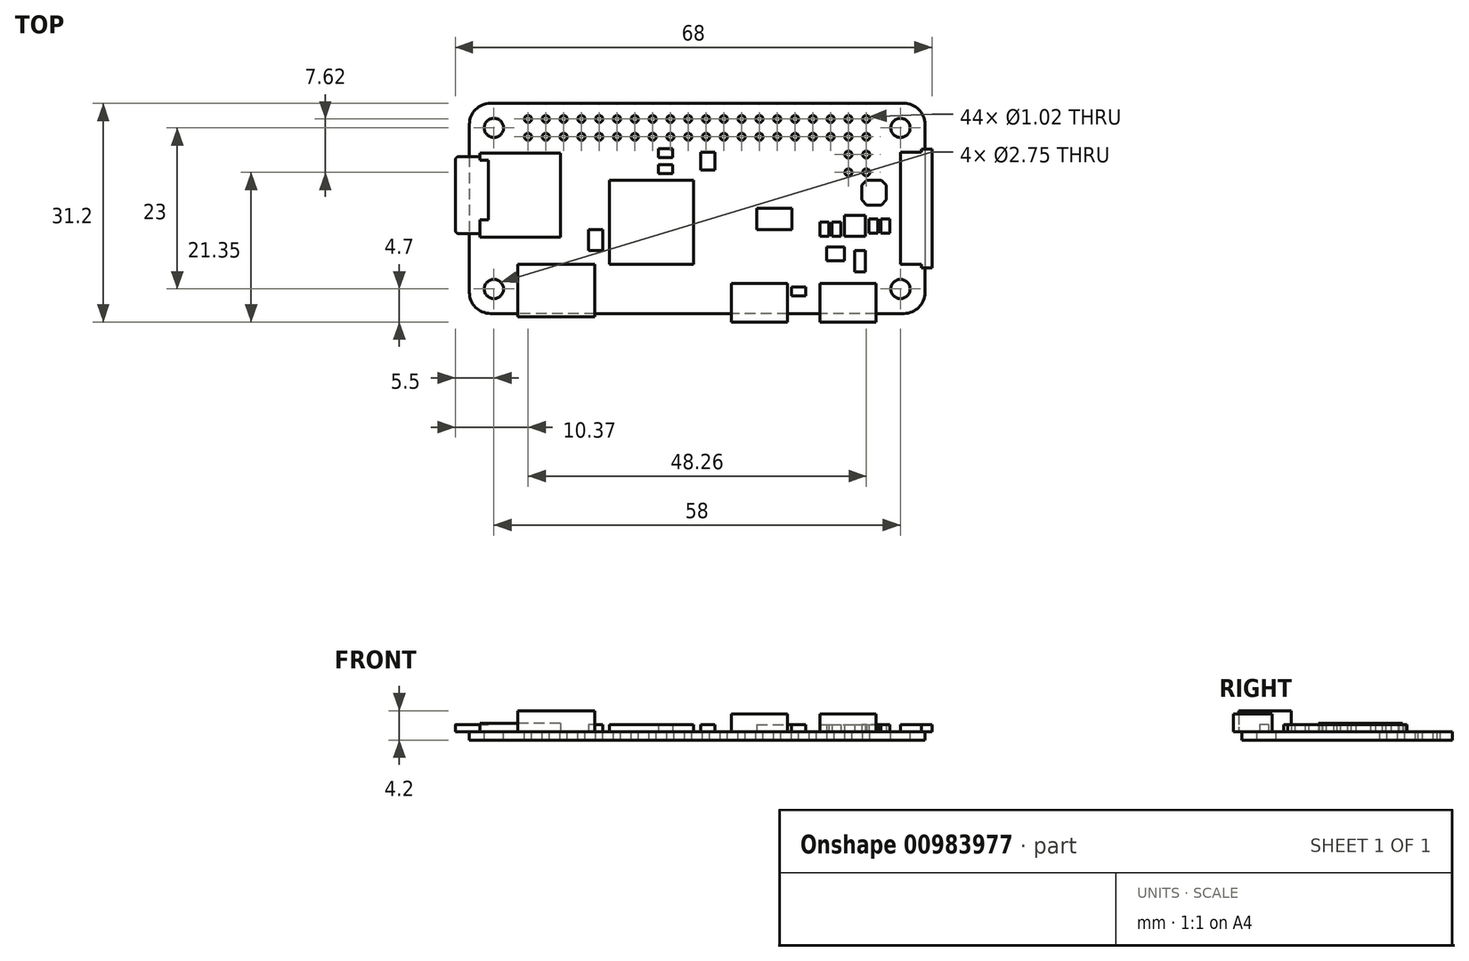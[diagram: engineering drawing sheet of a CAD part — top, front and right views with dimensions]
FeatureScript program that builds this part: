
annotation { "Feature Type Name" : "Feature", "Feature Type Description" : "" }
export const myFeature = defineFeature(function(context is Context, id is Id, definition is map)
    precondition{}
    {
        {
            var Q0;
            Q0=qCreatedBy(makeId("Top.planeOp"),FACE);
            var sketch = newSketch(context, id + "F0", { "sketchPlane" : qUnion([Q0])});
            skLineSegment(sketch, "E0.bottom", {"start": v(29.5, 15) * mm, "end": v(-29.5, 15) * mm});
            skLineSegment(sketch, "E0.top", {"start": v(29.5, -15) * mm, "end": v(-29.5, -15) * mm});
            skLineSegment(sketch, "E0.left", {"start": v(32.5, 12) * mm, "end": v(32.5, -12) * mm});
            skLineSegment(sketch, "E0.right", {"start": v(-32.5, 12) * mm, "end": v(-32.5, -12) * mm});
            skPoint(sketch, "E0.middle", {"position": v(0, 0) * mm});
            skPoint(sketch, "E1.visualSharp", {"position": v(-32.5, 15) * mm});
            skArc(sketch, "E1.filletArc", {"start": v(-29.5, 15) * mm, "mid": v(-31.62, 14.12) * mm, "end": v(-32.5, 12) * mm});
            skPoint(sketch, "E2.visualSharp", {"position": v(32.5, 15) * mm});
            skArc(sketch, "E2.filletArc", {"start": v(32.5, 12) * mm, "mid": v(31.62, 14.12) * mm, "end": v(29.5, 15) * mm});
            skPoint(sketch, "E3.visualSharp", {"position": v(32.5, -15) * mm});
            skArc(sketch, "E3.filletArc", {"start": v(29.5, -15) * mm, "mid": v(31.62, -14.12) * mm, "end": v(32.5, -12) * mm});
            skPoint(sketch, "E4.visualSharp", {"position": v(-32.5, -15) * mm});
            skArc(sketch, "E4.filletArc", {"start": v(-32.5, -12) * mm, "mid": v(-31.62, -14.12) * mm, "end": v(-29.5, -15) * mm});
            skLineSegment(sketch, "E5.bottom", {"start": v(29, 11.5) * mm, "end": v(-29, 11.5) * mm, "construction": true});
            skLineSegment(sketch, "E5.top", {"start": v(29, -11.5) * mm, "end": v(-29, -11.5) * mm, "construction": true});
            skLineSegment(sketch, "E5.left", {"start": v(29, 11.5) * mm, "end": v(29, -11.5) * mm, "construction": true});
            skLineSegment(sketch, "E5.right", {"start": v(-29, 11.5) * mm, "end": v(-29, -11.5) * mm, "construction": true});
            skCircle(sketch, "E6", {"center": v(29, 11.5) * mm, "radius": 3 * mm});
            skCircle(sketch, "E7", {"center": v(29, 11.5) * mm, "radius": 1.38 * mm});
            skCircle(sketch, "E8", {"center": v(-29, 11.5) * mm, "radius": 1.38 * mm});
            skCircle(sketch, "E9", {"center": v(-29, 11.5) * mm, "radius": 3 * mm});
            skCircle(sketch, "E10", {"center": v(-29, -11.5) * mm, "radius": 3 * mm});
            skCircle(sketch, "E11", {"center": v(-29, -11.5) * mm, "radius": 1.38 * mm});
            skCircle(sketch, "E12", {"center": v(29, -11.5) * mm, "radius": 1.38 * mm});
            skCircle(sketch, "E13", {"center": v(29, -11.5) * mm, "radius": 3 * mm});
            skCircle(sketch, "E14", {"center": v(24.13, 12.77) * mm, "radius": 0.5 * mm});
            skCircle(sketch, "E15", {"center": v(24.13, 10.23) * mm, "radius": 0.5 * mm});
            skLineSegment(sketch, "E16", {"start": v(24.13, 12.77) * mm, "end": v(24.13, 10.23) * mm, "construction": true});
            skPoint(sketch, "E17", {"position": v(24.13, 11.5) * mm});
            skCircle(sketch, "E18.1.0.0", {"center": v(21.59, 12.77) * mm, "radius": 0.5 * mm});
            skCircle(sketch, "E18.1.0.1", {"center": v(21.59, 10.23) * mm, "radius": 0.5 * mm});
            skCircle(sketch, "E18.2.0.0", {"center": v(19.05, 12.77) * mm, "radius": 0.5 * mm});
            skCircle(sketch, "E18.2.0.1", {"center": v(19.05, 10.23) * mm, "radius": 0.5 * mm});
            skCircle(sketch, "E18.3.0.0", {"center": v(16.5, 12.77) * mm, "radius": 0.5 * mm});
            skCircle(sketch, "E18.3.0.1", {"center": v(16.5, 10.23) * mm, "radius": 0.5 * mm});
            skCircle(sketch, "E18.4.0.0", {"center": v(13.97, 12.77) * mm, "radius": 0.5 * mm});
            skCircle(sketch, "E18.4.0.1", {"center": v(13.97, 10.23) * mm, "radius": 0.5 * mm});
            skCircle(sketch, "E18.5.0.0", {"center": v(11.43, 12.77) * mm, "radius": 0.5 * mm});
            skCircle(sketch, "E18.5.0.1", {"center": v(11.43, 10.23) * mm, "radius": 0.5 * mm});
            skCircle(sketch, "E18.6.0.0", {"center": v(8.89, 12.77) * mm, "radius": 0.5 * mm});
            skCircle(sketch, "E18.6.0.1", {"center": v(8.89, 10.23) * mm, "radius": 0.5 * mm});
            skCircle(sketch, "E18.7.0.0", {"center": v(6.35, 12.77) * mm, "radius": 0.5 * mm});
            skCircle(sketch, "E18.7.0.1", {"center": v(6.35, 10.23) * mm, "radius": 0.5 * mm});
            skCircle(sketch, "E18.8.0.0", {"center": v(3.8, 12.77) * mm, "radius": 0.5 * mm});
            skCircle(sketch, "E18.8.0.1", {"center": v(3.8, 10.23) * mm, "radius": 0.5 * mm});
            skCircle(sketch, "E18.9.0.0", {"center": v(1.27, 12.77) * mm, "radius": 0.5 * mm});
            skCircle(sketch, "E18.9.0.1", {"center": v(1.27, 10.23) * mm, "radius": 0.5 * mm});
            skCircle(sketch, "E18.10.0.0", {"center": v(-1.27, 12.77) * mm, "radius": 0.5 * mm});
            skCircle(sketch, "E18.10.0.1", {"center": v(-1.27, 10.23) * mm, "radius": 0.5 * mm});
            skCircle(sketch, "E18.11.0.0", {"center": v(-3.81, 12.77) * mm, "radius": 0.5 * mm});
            skCircle(sketch, "E18.11.0.1", {"center": v(-3.81, 10.23) * mm, "radius": 0.5 * mm});
            skCircle(sketch, "E18.12.0.0", {"center": v(-6.35, 12.77) * mm, "radius": 0.5 * mm});
            skCircle(sketch, "E18.12.0.1", {"center": v(-6.35, 10.23) * mm, "radius": 0.5 * mm});
            skCircle(sketch, "E18.13.0.0", {"center": v(-8.9, 12.77) * mm, "radius": 0.5 * mm});
            skCircle(sketch, "E18.13.0.1", {"center": v(-8.9, 10.23) * mm, "radius": 0.5 * mm});
            skCircle(sketch, "E18.14.0.0", {"center": v(-11.43, 12.77) * mm, "radius": 0.5 * mm});
            skCircle(sketch, "E18.14.0.1", {"center": v(-11.43, 10.23) * mm, "radius": 0.5 * mm});
            skCircle(sketch, "E18.15.0.0", {"center": v(-13.97, 12.77) * mm, "radius": 0.5 * mm});
            skCircle(sketch, "E18.15.0.1", {"center": v(-13.97, 10.23) * mm, "radius": 0.5 * mm});
            skCircle(sketch, "E18.16.0.0", {"center": v(-16.51, 12.77) * mm, "radius": 0.5 * mm});
            skCircle(sketch, "E18.16.0.1", {"center": v(-16.51, 10.23) * mm, "radius": 0.5 * mm});
            skCircle(sketch, "E18.17.0.0", {"center": v(-19.05, 12.77) * mm, "radius": 0.5 * mm});
            skCircle(sketch, "E18.17.0.1", {"center": v(-19.05, 10.23) * mm, "radius": 0.5 * mm});
            skCircle(sketch, "E18.18.0.0", {"center": v(-21.6, 12.77) * mm, "radius": 0.5 * mm});
            skCircle(sketch, "E18.18.0.1", {"center": v(-21.6, 10.23) * mm, "radius": 0.5 * mm});
            skCircle(sketch, "E18.19.0.0", {"center": v(-24.13, 12.77) * mm, "radius": 0.5 * mm});
            skCircle(sketch, "E18.19.0.1", {"center": v(-24.13, 10.23) * mm, "radius": 0.5 * mm});
            skLineSegment(sketch, "E18.direction1", {"start": v(24.13, 12.77) * mm, "end": v(21.59, 12.77) * mm, "construction": true});
            skCircle(sketch, "E19.1.0.0", {"center": v(21.59, 7.69) * mm, "radius": 0.5 * mm});
            skCircle(sketch, "E19.1.0.1", {"center": v(24.13, 7.69) * mm, "radius": 0.5 * mm});
            skCircle(sketch, "E19.1.0.2", {"center": v(24.13, 5.15) * mm, "radius": 0.5 * mm});
            skCircle(sketch, "E19.1.0.3", {"center": v(21.59, 5.15) * mm, "radius": 0.5 * mm});
            skLineSegment(sketch, "E19.direction1", {"start": v(21.59, 12.77) * mm, "end": v(21.59, 7.69) * mm, "construction": true});
            skSolve(sketch);
        }
        {
            var Q0;
            Q0=qCreatedBy(makeId("Top.planeOp"),FACE);
            var sketch = newSketch(context, id + "F1", { "sketchPlane" : qUnion([Q0])});
            skLineSegment(sketch, "E20.bottom", {"start": v(33.5, -8.5) * mm, "end": v(32, -8.5) * mm});
            skLineSegment(sketch, "E20.top", {"start": v(33.5, 8.5) * mm, "end": v(32, 8.5) * mm});
            skLineSegment(sketch, "E20.left", {"start": v(33.5, -8.5) * mm, "end": v(33.5, 8.5) * mm});
            skLineSegment(sketch, "E20.right", {"start": v(32, -8.5) * mm, "end": v(32, 8.5) * mm});
            skPoint(sketch, "E20.middle", {"position": v(32.75, 0) * mm});
            skLineSegment(sketch, "E21.bottom", {"start": v(-14.6, -15.5) * mm, "end": v(-25.6, -15.5) * mm});
            skLineSegment(sketch, "E21.top", {"start": v(-14.6, -8) * mm, "end": v(-25.6, -8) * mm});
            skLineSegment(sketch, "E21.left", {"start": v(-14.6, -15.5) * mm, "end": v(-14.6, -8) * mm});
            skLineSegment(sketch, "E21.right", {"start": v(-25.6, -15.5) * mm, "end": v(-25.6, -8) * mm});
            skPoint(sketch, "E21.middle", {"position": v(-20.1, -11.75) * mm});
            skLineSegment(sketch, "E22.bottom", {"start": v(12.9, -16.2) * mm, "end": v(4.9, -16.2) * mm});
            skLineSegment(sketch, "E22.top", {"start": v(12.9, -10.7) * mm, "end": v(4.9, -10.7) * mm});
            skLineSegment(sketch, "E22.left", {"start": v(12.9, -16.2) * mm, "end": v(12.9, -10.7) * mm});
            skLineSegment(sketch, "E22.right", {"start": v(4.9, -16.2) * mm, "end": v(4.9, -10.7) * mm});
            skPoint(sketch, "E22.middle", {"position": v(8.9, -13.45) * mm});
            skLineSegment(sketch, "E23.bottom", {"start": v(25.5, -16.2) * mm, "end": v(17.5, -16.2) * mm});
            skLineSegment(sketch, "E23.top", {"start": v(25.5, -10.7) * mm, "end": v(17.5, -10.7) * mm});
            skLineSegment(sketch, "E23.left", {"start": v(25.5, -16.2) * mm, "end": v(25.5, -10.7) * mm});
            skLineSegment(sketch, "E23.right", {"start": v(17.5, -16.2) * mm, "end": v(17.5, -10.7) * mm});
            skPoint(sketch, "E23.middle", {"position": v(21.5, -13.45) * mm});
            skLineSegment(sketch, "E24.bottom", {"start": v(-19.5, 7.9) * mm, "end": v(-31, 7.9) * mm});
            skLineSegment(sketch, "E24.top", {"start": v(-19.5, -4.1) * mm, "end": v(-31, -4.1) * mm});
            skLineSegment(sketch, "E24.left", {"start": v(-19.5, 7.9) * mm, "end": v(-19.5, -4.1) * mm});
            skLineSegment(sketch, "E24.right", {"start": v(-31, 7.9) * mm, "end": v(-31, -4.1) * mm});
            skPoint(sketch, "E24.middle", {"position": v(-25.25, 1.9) * mm});
            skLineSegment(sketch, "E25", {"start": v(-31, 7.4) * mm, "end": v(-34, 7.4) * mm});
            skLineSegment(sketch, "E26", {"start": v(-34.5, 6.9) * mm, "end": v(-34.5, -3.1) * mm});
            skLineSegment(sketch, "E27", {"start": v(-34, -3.6) * mm, "end": v(-31, -3.6) * mm});
            skPoint(sketch, "E28.visualSharp", {"position": v(-34.5, 7.4) * mm});
            skArc(sketch, "E28.filletArc", {"start": v(-34, 7.4) * mm, "mid": v(-34.35, 7.25) * mm, "end": v(-34.5, 6.9) * mm});
            skPoint(sketch, "E29.visualSharp", {"position": v(-34.5, -3.6) * mm});
            skArc(sketch, "E29.filletArc", {"start": v(-34.5, -3.1) * mm, "mid": v(-34.35, -3.45) * mm, "end": v(-34, -3.6) * mm});
            skPoint(sketch, "E30", {"position": v(-34.5, 1.9) * mm});
            skLineSegment(sketch, "E31", {"start": v(-31, 6.9) * mm, "end": v(-29.8, 6.9) * mm});
            skLineSegment(sketch, "E32", {"start": v(-29.8, 6.9) * mm, "end": v(-29.8, -1.6) * mm});
            skLineSegment(sketch, "E33", {"start": v(-29.8, -1.6) * mm, "end": v(-31, -1.6) * mm});
            skLineSegment(sketch, "E34", {"start": v(32, 8) * mm, "end": v(29, 8) * mm});
            skLineSegment(sketch, "E35", {"start": v(29, 8) * mm, "end": v(29, -8) * mm});
            skLineSegment(sketch, "E36", {"start": v(29, -8) * mm, "end": v(32, -8) * mm});
            skLineSegment(sketch, "E37", {"start": v(32.75, 0) * mm, "end": v(29, 0) * mm, "construction": true});
            skSolve(sketch);
        }
        {
            var Q0;
            Q0=qCreatedBy(makeId("Top.planeOp"),FACE);
            var sketch = newSketch(context, id + "F2", { "sketchPlane" : qUnion([Q0])});
            skLineSegment(sketch, "E38.bottom", {"start": v(-12.5, -8) * mm, "end": v(-0.5, -8) * mm});
            skLineSegment(sketch, "E38.top", {"start": v(-12.5, 4) * mm, "end": v(-0.5, 4) * mm});
            skLineSegment(sketch, "E38.left", {"start": v(-12.5, -8) * mm, "end": v(-12.5, 4) * mm});
            skLineSegment(sketch, "E38.right", {"start": v(-0.5, -8) * mm, "end": v(-0.5, 4) * mm});
            skLineSegment(sketch, "E39.bottom", {"start": v(-5.53, 8.54) * mm, "end": v(-3.5, 8.54) * mm});
            skLineSegment(sketch, "E39.top", {"start": v(-5.53, 7.27) * mm, "end": v(-3.5, 7.27) * mm});
            skLineSegment(sketch, "E39.left", {"start": v(-5.53, 8.54) * mm, "end": v(-5.53, 7.27) * mm});
            skLineSegment(sketch, "E39.right", {"start": v(-3.5, 8.54) * mm, "end": v(-3.5, 7.27) * mm});
            skLineSegment(sketch, "E40.bottom", {"start": v(-5.53, 6.27) * mm, "end": v(-3.5, 6.27) * mm});
            skLineSegment(sketch, "E40.top", {"start": v(-5.53, 5) * mm, "end": v(-3.5, 5) * mm});
            skLineSegment(sketch, "E40.left", {"start": v(-5.53, 6.27) * mm, "end": v(-5.53, 5) * mm});
            skLineSegment(sketch, "E40.right", {"start": v(-3.5, 6.27) * mm, "end": v(-3.5, 5) * mm});
            skLineSegment(sketch, "E41.bottom", {"start": v(13.47, -11.23) * mm, "end": v(15.5, -11.23) * mm});
            skLineSegment(sketch, "E41.top", {"start": v(13.47, -12.5) * mm, "end": v(15.5, -12.5) * mm});
            skLineSegment(sketch, "E41.left", {"start": v(13.47, -11.23) * mm, "end": v(13.47, -12.5) * mm});
            skLineSegment(sketch, "E41.right", {"start": v(15.5, -11.23) * mm, "end": v(15.5, -12.5) * mm});
            skLineSegment(sketch, "E42.bottom", {"start": v(17.5, -1.97) * mm, "end": v(18.77, -1.97) * mm});
            skLineSegment(sketch, "E42.top", {"start": v(17.5, -4) * mm, "end": v(18.77, -4) * mm});
            skLineSegment(sketch, "E42.left", {"start": v(17.5, -1.97) * mm, "end": v(17.5, -4) * mm});
            skLineSegment(sketch, "E42.right", {"start": v(18.77, -1.97) * mm, "end": v(18.77, -4) * mm});
            skLineSegment(sketch, "E43.bottom", {"start": v(19.25, -1.97) * mm, "end": v(20.52, -1.97) * mm});
            skLineSegment(sketch, "E43.top", {"start": v(19.25, -4) * mm, "end": v(20.52, -4) * mm});
            skLineSegment(sketch, "E43.left", {"start": v(19.25, -1.97) * mm, "end": v(19.25, -4) * mm});
            skLineSegment(sketch, "E43.right", {"start": v(20.52, -1.97) * mm, "end": v(20.52, -4) * mm});
            skLineSegment(sketch, "E44.bottom", {"start": v(24.48, -1.48) * mm, "end": v(25.75, -1.48) * mm});
            skLineSegment(sketch, "E44.top", {"start": v(24.48, -3.52) * mm, "end": v(25.75, -3.52) * mm});
            skLineSegment(sketch, "E44.left", {"start": v(24.48, -1.48) * mm, "end": v(24.48, -3.52) * mm});
            skLineSegment(sketch, "E44.right", {"start": v(25.75, -1.48) * mm, "end": v(25.75, -3.52) * mm});
            skLineSegment(sketch, "E45.bottom", {"start": v(26.23, -1.48) * mm, "end": v(27.5, -1.48) * mm});
            skLineSegment(sketch, "E45.top", {"start": v(26.23, -3.52) * mm, "end": v(27.5, -3.52) * mm});
            skLineSegment(sketch, "E45.left", {"start": v(26.23, -1.48) * mm, "end": v(26.23, -3.52) * mm});
            skLineSegment(sketch, "E45.right", {"start": v(27.5, -1.48) * mm, "end": v(27.5, -3.52) * mm});
            skLineSegment(sketch, "E46.bottom", {"start": v(-13.5, -3) * mm, "end": v(-15.5, -3) * mm});
            skLineSegment(sketch, "E46.top", {"start": v(-13.5, -6) * mm, "end": v(-15.5, -6) * mm});
            skLineSegment(sketch, "E46.left", {"start": v(-13.5, -3) * mm, "end": v(-13.5, -6) * mm});
            skLineSegment(sketch, "E46.right", {"start": v(-15.5, -3) * mm, "end": v(-15.5, -6) * mm});
            skLineSegment(sketch, "E47.bottom", {"start": v(8.5, 0) * mm, "end": v(13.5, 0) * mm});
            skLineSegment(sketch, "E47.top", {"start": v(8.5, -3) * mm, "end": v(13.5, -3) * mm});
            skLineSegment(sketch, "E47.left", {"start": v(8.5, 0) * mm, "end": v(8.5, -3) * mm});
            skLineSegment(sketch, "E47.right", {"start": v(13.5, 0) * mm, "end": v(13.5, -3) * mm});
            skLineSegment(sketch, "E48.bottom", {"start": v(21, -1) * mm, "end": v(24, -1) * mm});
            skLineSegment(sketch, "E48.top", {"start": v(21, -4) * mm, "end": v(24, -4) * mm});
            skLineSegment(sketch, "E48.left", {"start": v(21, -1) * mm, "end": v(21, -4) * mm});
            skLineSegment(sketch, "E48.right", {"start": v(24, -1) * mm, "end": v(24, -4) * mm});
            skLineSegment(sketch, "E49.bottom", {"start": v(0.5, 8) * mm, "end": v(2.5, 8) * mm});
            skLineSegment(sketch, "E49.top", {"start": v(0.5, 5.5) * mm, "end": v(2.5, 5.5) * mm});
            skLineSegment(sketch, "E49.left", {"start": v(0.5, 8) * mm, "end": v(0.5, 5.5) * mm});
            skLineSegment(sketch, "E49.right", {"start": v(2.5, 8) * mm, "end": v(2.5, 5.5) * mm});
            skLineSegment(sketch, "E50.bottom", {"start": v(18.5, -5.5) * mm, "end": v(21, -5.5) * mm});
            skLineSegment(sketch, "E50.top", {"start": v(18.5, -7.5) * mm, "end": v(21, -7.5) * mm});
            skLineSegment(sketch, "E50.left", {"start": v(18.5, -5.5) * mm, "end": v(18.5, -7.5) * mm});
            skLineSegment(sketch, "E50.right", {"start": v(21, -5.5) * mm, "end": v(21, -7.5) * mm});
            skLineSegment(sketch, "E51.bottom", {"start": v(22.48, -6) * mm, "end": v(24, -6) * mm});
            skLineSegment(sketch, "E51.top", {"start": v(22.48, -9.05) * mm, "end": v(24, -9.05) * mm});
            skLineSegment(sketch, "E51.left", {"start": v(22.48, -6) * mm, "end": v(22.48, -9.05) * mm});
            skLineSegment(sketch, "E51.right", {"start": v(24, -6) * mm, "end": v(24, -9.05) * mm});
            skLineSegment(sketch, "E52", {"start": v(24, -2.5) * mm, "end": v(24.48, -2.5) * mm, "construction": true});
            skLineSegment(sketch, "E53", {"start": v(26.23, -3.52) * mm, "end": v(25.75, -3.52) * mm, "construction": true});
            skLineSegment(sketch, "E54", {"start": v(21, -4) * mm, "end": v(20.52, -4) * mm, "construction": true});
            skLineSegment(sketch, "E55", {"start": v(19.25, -4) * mm, "end": v(18.77, -4) * mm, "construction": true});
            skLineSegment(sketch, "E56", {"start": v(23.5, 3.3) * mm, "end": v(23.5, 1.2) * mm});
            skLineSegment(sketch, "E57", {"start": v(23.5, 1.2) * mm, "end": v(24.2, 0.5) * mm});
            skLineSegment(sketch, "E58", {"start": v(24.2, 0.5) * mm, "end": v(26.3, 0.5) * mm});
            skLineSegment(sketch, "E59", {"start": v(26.3, 0.5) * mm, "end": v(27, 1.2) * mm});
            skLineSegment(sketch, "E60", {"start": v(27, 1.2) * mm, "end": v(27, 3.3) * mm});
            skLineSegment(sketch, "E61", {"start": v(27, 3.3) * mm, "end": v(26.3, 4) * mm});
            skLineSegment(sketch, "E62", {"start": v(26.3, 4) * mm, "end": v(24.2, 4) * mm});
            skLineSegment(sketch, "E63", {"start": v(24.2, 4) * mm, "end": v(23.5, 3.3) * mm});
            skSolve(sketch);
        }
        {
            var Q0;
            Q0=qSketchRegion(id+"F0",true);
            var Q1;
            Q1=makeQuery(id+"F0.imprint","IMPRINT",FACE,{"disambiguationData":[TD([[makeQuery(id+"F0.imprint","IMPRINT",EDGE,{"derivedFrom":sQuery(id+"F0.wireOp",EDGE,"E10")}),1.0]])]});
            var Q2;
            Q2=makeQuery(id+"F0.imprint","IMPRINT",FACE,{"disambiguationData":[TD([[makeQuery(id+"F0.imprint","IMPRINT",EDGE,{"derivedFrom":sQuery(id+"F0.wireOp",EDGE,"E8")}),-1.0]])]});
            var Q3;
            Q3=makeQuery(id+"F0.imprint","IMPRINT",FACE,{"disambiguationData":[TD([[makeQuery(id+"F0.imprint","IMPRINT",EDGE,{"derivedFrom":sQuery(id+"F0.wireOp",EDGE,"E6")}),1.0]])]});
            var Q4;
            Q4=makeQuery(id+"F0.imprint","IMPRINT",FACE,{"disambiguationData":[TD([[makeQuery(id+"F0.imprint","IMPRINT",EDGE,{"derivedFrom":sQuery(id+"F0.wireOp",EDGE,"E12")}),-1.0]])]});
            extrude(context, id + "F3", {"entities" : qUnion([Q0, Q1, Q2, Q3, Q4]), "oppositeDirection" : true, "depth" : 1.2 * mm, "offsetDistance" : 25 * mm});
        }
        {
            var Q0;
            Q0=makeQuery(id+"F1.imprint","IMPRINT",FACE,{"disambiguationData":[TD([[makeQuery(id+"F1.imprint","IMPRINT",EDGE,{"derivedFrom":sQuery(id+"F1.wireOp",EDGE,"E20.bottom")}),-1.0]])]});
            extrude(context, id + "F4", {"entities" : qUnion([Q0]), "operationType" : NewBodyOperationType.ADD, "depth" : 1 * mm, "offsetDistance" : 25 * mm});
        }
        {
            var Q0;
            {var subQ0=sQuery(id+"F1.wireOp",EDGE,"E34");Q0=makeQuery(id+"F1.imprint","IMPRINT",FACE,{"disambiguationData":[TD([[makeQuery(id+"F1.imprint","IMPRINT",EDGE,{"derivedFrom":subQ0}),1.0]])]});}
            extrude(context, id + "F5", {"entities" : qUnion([Q0]), "operationType" : NewBodyOperationType.ADD, "depth" : 1 * mm, "offsetDistance" : 25 * mm});
        }
        {
            var Q0;
            Q0=makeQuery(id+"F1.imprint","IMPRINT",FACE,{"disambiguationData":[TD([[makeQuery(id+"F1.imprint","IMPRINT",EDGE,{"derivedFrom":sQuery(id+"F1.wireOp",EDGE,"E23.bottom")}),-1.0]])]});
            var Q1;
            Q1=makeQuery(id+"F1.imprint","IMPRINT",FACE,{"disambiguationData":[TD([[makeQuery(id+"F1.imprint","IMPRINT",EDGE,{"derivedFrom":sQuery(id+"F1.wireOp",EDGE,"E22.bottom")}),-1.0]])]});
            extrude(context, id + "F6", {"entities" : qUnion([Q0, Q1]), "operationType" : NewBodyOperationType.ADD, "depth" : 2.5 * mm, "offsetDistance" : 25 * mm});
        }
        {
            var Q0;
            Q0=makeQuery(id+"F1.imprint","IMPRINT",FACE,{"disambiguationData":[TD([[makeQuery(id+"F1.imprint","IMPRINT",EDGE,{"derivedFrom":sQuery(id+"F1.wireOp",EDGE,"E21.bottom")}),-1.0]])]});
            extrude(context, id + "F7", {"entities" : qUnion([Q0]), "operationType" : NewBodyOperationType.ADD, "depth" : 3 * mm, "offsetDistance" : 25 * mm});
        }
        {
            var Q0;
            {var subQ1=sQuery(id+"F1.wireOp",EDGE,"E24.bottom");Q0=makeQuery(id+"F1.imprint","IMPRINT",FACE,{"disambiguationData":[TD([[makeQuery(id+"F1.imprint","IMPRINT",EDGE,{"derivedFrom":subQ1}),1.0]])]});}
            extrude(context, id + "F8", {"entities" : qUnion([Q0]), "operationType" : NewBodyOperationType.ADD, "depth" : 1.2 * mm, "offsetDistance" : 25 * mm});
        }
        {
            var Q0;
            {var subQ0=sQuery(id+"F1.wireOp",EDGE,"E31");Q0=makeQuery(id+"F1.imprint","IMPRINT",FACE,{"disambiguationData":[TD([[makeQuery(id+"F1.imprint","IMPRINT",EDGE,{"derivedFrom":subQ0}),-1.0]])]});}
            var Q1;
            {var subQ0=sQuery(id+"F1.wireOp",EDGE,"E25");Q1=makeQuery(id+"F1.imprint","IMPRINT",FACE,{"disambiguationData":[TD([[makeQuery(id+"F1.imprint","IMPRINT",EDGE,{"derivedFrom":subQ0}),1.0]])]});}
            extrude(context, id + "F9", {"entities" : qUnion([Q0, Q1]), "operationType" : NewBodyOperationType.ADD, "depth" : 1 * mm, "offsetDistance" : 25 * mm});
        }
        {
            var Q0;
            Q0=qSketchRegion(id+"F2",true);
            extrude(context, id + "F10", {"entities" : qUnion([Q0]), "operationType" : NewBodyOperationType.ADD, "depth" : 1 * mm, "offsetDistance" : 25 * mm});
        }
    });
